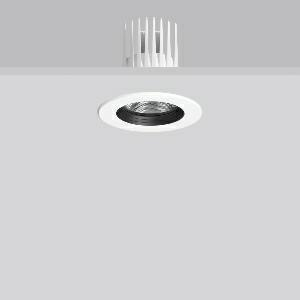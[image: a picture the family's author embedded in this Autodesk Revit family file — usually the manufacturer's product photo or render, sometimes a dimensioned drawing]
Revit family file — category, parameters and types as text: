
# Revit family: heledon_mini_e_901740_002_76_d988
name_source: partatom
category: Lighting Fixtures
units: mm (PartAtom-declared; Revit-internal decimal feet)

## family parameters
Cut with Voids When Loaded = No
Host = Face
Light Source = No
Part Type = Normal
Room Calculation Point = No
Round Connector Dimension = Use Diameter
Shared = No

## types (1)
- HELEDON mini E (1 x LED Modul 930, 2500 lm, 3000)
    Apparent Load = 20 VA
    Approval mark = CE
    CIE Flux Codes = 100 100 100 100 100
    Color Rendering = 90
    Color Temperature = 3000
    Default Elevation = 1800 mm
    Description = Series: HELEDON mini
Round recessed downlight. Housing: die-cast aluminium, powder-coated. Black plastic ring and recessed LED to prevent glare from the side. Optical assembly with reflector made of MIRO-Silver with 98% total light reflection for outstanding efficiency - can be changed without tools. Best colour rendering index Ra>90. Suitable for Recessed ceiling mounting. Installation without tools thanks to spring fastening system. Including separate LED converter with connecting cable 600 mm.High quality converter without flickering and stroboscopic effect. Through-wiring box (5 pole) available as accessory. The following accessories can be mounted without use of tools: interchangeable lenses, decorative glasses, honeycomb louvre, clear and frosted diffusers, white interchangeable plastic ring. 
Colour: traffic white, matt (RAL 9016)
Diameter: 124 mm
Height: 3 mm
Cut-out diameter: 114 mm
Recess height: 170 mm
Luminaire: recess height: 120 mm
Lamp: LED
Socket: without socket
Colour temperature: 3000K
Colour rendering index (CRI): 92
System power: 20 W
Rated luminous flux: 2500 lm
Luminous efficiency: 125 lm/W
Control gear: Converter, dimmable, DALI
Protection class: II
Type of protection: IP 20
    Height = 0 mm  [stored 0 ft]
    Lamp = 1 x LED Modul 930
    Lamp Light Flux = 2500 lm
    Lamp count = 1
    Length = 124 mm  [stored 0.406824 ft]
    Lifetime = 50000 h
    Luminous efficacy = 125 lm/W
    Manufacturer = RZB
    ModVariant = No
    Model = 901740.002.76
    Mounting Place = Ceiling
    Mounting Type = Recessed
    Number of Poles = 1
    OnlyDefault = Yes
    Power Factor = 1
    Product Name = HELEDON mini E
    Product group = Recessed downlights
    ProductGroupID = 402
    Protection Class = Protection class II
    Protection Degree = IP 20
    RLX_Detail_Level = 1
    RLX_Emergency_Light_Flux = 0 lm
    RLX_Emergency_Type = 0
    RLX_Emergency_Type_DB = No
    RlxData = <blob elided: 126017 chars, md5=3e9a5815>
    Socket = socket
    Standby Power = 0 W
    System Light Flux = 2500 lm
    System Power = 20 W
    Type Comments = Product without accessories
    Type Image = 901657.002.jpg
    URL = http://relux.com
    VarID = ---
    Voltage = 230 V
    Voltage Range = 220-240 V
    Weight = 0.00 kg
    Width = 0 mm  [stored 0 ft]

note: [stored X ft] marks values corroborated as IEEE doubles in the binary element streams (Revit-internal decimal feet)

## geometry (parser evidence)
native form markers: Blend x4, Sweep x13
no freeform markers — native parametric forms only
